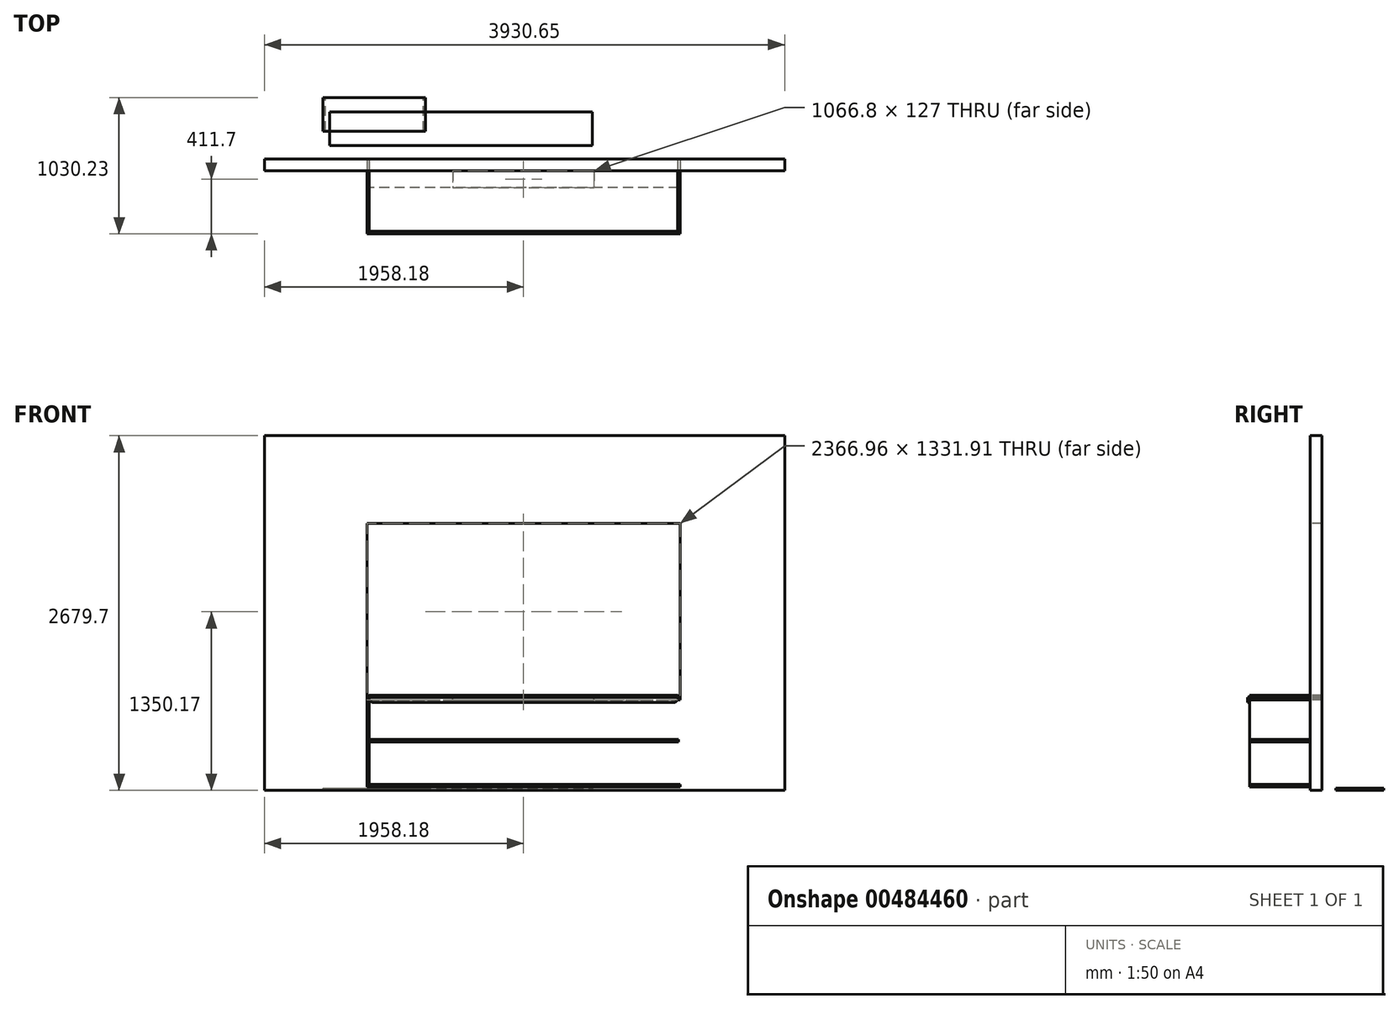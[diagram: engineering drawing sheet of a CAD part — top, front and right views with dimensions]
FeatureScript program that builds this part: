
annotation { "Feature Type Name" : "Feature", "Feature Type Description" : "" }
export const myFeature = defineFeature(function(context is Context, id is Id, definition is map)
    precondition{}
    {
        {
            assignVariable(context, id + "F0", {"name" : "windowwidth", "anyValue" : 2366.96 * mm});
        }
        {
            assignVariable(context, id + "F1", {"name" : "windowtofloor", "anyValue" : 684.2 * mm});
        }
        {
            assignVariable(context, id + "F2", {"name" : "materialthickness", "anyValue" : 18 * mm});
        }
        {
            assignVariable(context, id + "F3", {"name" : "trim", "anyValue" : 38.1 * mm});
        }
        {
            assignVariable(context, id + "F4", {"name" : "dadodepth", "anyValue" : getVariable(context, 'materialthickness') / 3});
        }
        {
            var Q0;
            Q0=qCreatedBy(makeId("Front.planeOp"),FACE);
            var sketch = newSketch(context, id + "F5", { "sketchPlane" : qUnion([Q0])});
            skLineSegment(sketch, "E0.bottom", {"start": v(-1875.03, 2679.7) * mm, "end": v(2055.62, 2679.7) * mm});
            skLineSegment(sketch, "E0.top", {"start": v(-1875.03, 0) * mm, "end": v(2055.62, 0) * mm});
            skLineSegment(sketch, "E0.left", {"start": v(-1875.03, 2679.7) * mm, "end": v(-1875.03, 0) * mm});
            skLineSegment(sketch, "E0.right", {"start": v(2055.62, 2679.7) * mm, "end": v(2055.62, 0) * mm});
            skSolve(sketch);
        }
        {
            var Q0;
            Q0 = qSketchRegion(id + "F5", true);
            extrude(context, id + "F6", {"entities" : qUnion([Q0]), "depth" : 88.9 * mm});
        }
        {
            var Q0;
            Q0=makeQuery(id+"F6.opExtrude","CAP_FACE",FACE,{"disambiguationData":[OSD([sQuery(id+"F5.wireOp",EDGE,"E0.bottom"),sQuery(id+"F5.wireOp",EDGE,"E0.top"),sQuery(id+"F5.wireOp",EDGE,"E0.left"),sQuery(id+"F5.wireOp",EDGE,"E0.right")])],"isStart":false});
            var sketch = newSketch(context, id + "F7", { "sketchPlane" : qUnion([Q0])});
            skLineSegment(sketch, "E1.bottom", {"start": v(-1100.33, 2016.13) * mm, "end": v(1266.63, 2016.13) * mm});
            skLineSegment(sketch, "E1.top", {"start": v(-1100.33, 684.21) * mm, "end": v(1266.63, 684.21) * mm});
            skLineSegment(sketch, "E1.left", {"start": v(-1100.33, 2016.12) * mm, "end": v(-1100.33, 684.21) * mm});
            skLineSegment(sketch, "E1.right", {"start": v(1266.63, 2016.12) * mm, "end": v(1266.63, 684.21) * mm});
            skSolve(sketch);
        }
        {
            var Q0;
            Q0 = qSketchRegion(id + "F7", true);
            extrude(context, id + "F8", {"entities" : qUnion([Q0]), "operationType" : NewBodyOperationType.REMOVE, "oppositeDirection" : true, "depth" : 101.6 * mm});
        }
        {
            var Q0;
            Q0=makeQuery(id+"F8.boolean.opBoolean","COPY",FACE,{"derivedFrom":makeQuery(id+"F8.opExtrude","SWEPT_FACE",FACE,{"disambiguationData":[OSD([sQuery(id+"F7.wireOp",EDGE,"E1.top")])]})});
            var sketch = newSketch(context, id + "F9", { "sketchPlane" : qUnion([Q0])});
            skPoint(sketch, "E2.oppositeSnap0", {"position": v(1266.63, -44.45) * mm});
            skLineSegment(sketch, "E2.bottom", {"start": v(-1100.33, 0) * mm, "end": v(1266.63, 0) * mm});
            skLineSegment(sketch, "E2.top", {"start": v(-1100.33, -546.1) * mm, "end": v(1266.63, -546.1) * mm});
            skLineSegment(sketch, "E2.left", {"start": v(-1100.33, 0) * mm, "end": v(-1100.33, -546.1) * mm});
            skLineSegment(sketch, "E2.right", {"start": v(1266.63, 0) * mm, "end": v(1266.63, -546.1) * mm});
            skSolve(sketch);
        }
        {
            var Q0;
            Q0 = qSketchRegion(id + "F9", true);
            extrude(context, id + "F10", {"entities" : qUnion([Q0]), "depth" : getVariable(context, 'materialthickness')});
        }
        {
            var Q0;
            Q0=makeQuery(id+"F10.opExtrude","CAP_FACE",FACE,{"disambiguationData":[OSD([sQuery(id+"F9.wireOp",EDGE,"E2.bottom"),sQuery(id+"F9.wireOp",EDGE,"E2.top"),sQuery(id+"F9.wireOp",EDGE,"E2.left"),sQuery(id+"F9.wireOp",EDGE,"E2.right")])],"isStart":true});
            var sketch = newSketch(context, id + "F11", { "sketchPlane" : qUnion([Q0])});
            skLineSegment(sketch, "E3.bottom", {"start": v(-1100.33, 546.1) * mm, "end": v(-1082.33, 546.1) * mm});
            skLineSegment(sketch, "E3.top", {"start": v(-1100.33, 0) * mm, "end": v(-1082.33, 0) * mm});
            skLineSegment(sketch, "E3.left", {"start": v(-1100.33, 546.1) * mm, "end": v(-1100.33, 0) * mm});
            skLineSegment(sketch, "E3.right", {"start": v(-1082.33, 546.1) * mm, "end": v(-1082.33, 0) * mm});
            skLineSegment(sketch, "E4.bottom", {"start": v(1266.63, 546.1) * mm, "end": v(1248.63, 546.1) * mm});
            skLineSegment(sketch, "E4.top", {"start": v(1266.63, 0) * mm, "end": v(1248.63, 0) * mm});
            skLineSegment(sketch, "E4.left", {"start": v(1266.63, 546.1) * mm, "end": v(1266.63, 0) * mm});
            skLineSegment(sketch, "E4.right", {"start": v(1248.63, 546.1) * mm, "end": v(1248.63, 0) * mm});
            skSolve(sketch);
        }
        {
            var Q0;
            Q0 = qSketchRegion(id + "F11", true);
            extrude(context, id + "F12", {"entities" : qUnion([Q0]), "operationType" : NewBodyOperationType.REMOVE, "oppositeDirection" : true, "depth" : getVariable(context, 'dadodepth')});
        }
        {
            var Q0;
            Q0=makeQuery(id+"F10.opExtrude","CAP_FACE",FACE,{"disambiguationData":[OSD([sQuery(id+"F9.wireOp",EDGE,"E2.bottom"),sQuery(id+"F9.wireOp",EDGE,"E2.top"),sQuery(id+"F9.wireOp",EDGE,"E2.left"),sQuery(id+"F9.wireOp",EDGE,"E2.right")])],"isStart":false});
            var sketch = newSketch(context, id + "F13", { "sketchPlane" : qUnion([Q0])});
            skLineSegment(sketch, "E5", {"start": v(83.15, -546.1) * mm, "end": v(83.15, 0) * mm, "construction": true});
            skLineSegment(sketch, "E6.bottom", {"start": v(-450.25, -88.9) * mm, "end": v(616.55, -88.9) * mm});
            skLineSegment(sketch, "E6.top", {"start": v(-450.25, -215.9) * mm, "end": v(616.55, -215.9) * mm});
            skLineSegment(sketch, "E6.left", {"start": v(-450.25, -88.9) * mm, "end": v(-450.25, -215.9) * mm});
            skLineSegment(sketch, "E6.right", {"start": v(616.55, -88.9) * mm, "end": v(616.55, -215.9) * mm});
            skPoint(sketch, "E6.middle", {"position": v(83.15, -273.05) * mm});
            skSolve(sketch);
        }
        {
            var Q0;
            Q0 = qSketchRegion(id + "F13", true);
            extrude(context, id + "F14", {"entities" : qUnion([Q0]), "operationType" : NewBodyOperationType.REMOVE, "oppositeDirection" : true, "depth" : 25.4 * mm});
        }
        {
            var Q0;
            Q0=makeQuery(id+"F12.boolean.opBoolean","COPY",FACE,{"derivedFrom":makeQuery(id+"F12.opExtrude","CAP_FACE",FACE,{"disambiguationData":[OSD([sQuery(id+"F11.wireOp",EDGE,"E3.bottom"),sQuery(id+"F11.wireOp",EDGE,"E3.top"),sQuery(id+"F11.wireOp",EDGE,"E3.left"),sQuery(id+"F11.wireOp",EDGE,"E3.right")])],"isStart":false})});
            var sketch = newSketch(context, id + "F15", { "sketchPlane" : qUnion([Q0])});
            skLineSegment(sketch, "E7.bottom", {"start": v(-1100.33, 546.1) * mm, "end": v(-1082.33, 546.1) * mm});
            skLineSegment(sketch, "E7.top", {"start": v(-1100.33, 88.9) * mm, "end": v(-1082.33, 88.9) * mm});
            skLineSegment(sketch, "E7.left", {"start": v(-1100.33, 546.1) * mm, "end": v(-1100.33, 88.9) * mm});
            skLineSegment(sketch, "E7.right", {"start": v(-1082.33, 546.1) * mm, "end": v(-1082.33, 88.9) * mm});
            skSolve(sketch);
        }
        {
            var Q0;
            Q0 = qSketchRegion(id + "F15", true);
            extrude(context, id + "F16", {"entities" : qUnion([Q0]), "depth" : getVariable(context, 'windowtofloor') + getVariable(context, 'dadodepth') - (getVariable(context, 'materialthickness') - getVariable(context, 'dadodepth')) - (getVariable(context, 'trim') - getVariable(context, 'dadodepth'))});
        }
        {
            var Q0;
            Q0=makeQuery(id+"F10.opExtrude","SWEPT_FACE",FACE,{"disambiguationData":[OSD([sQuery(id+"F9.wireOp",EDGE,"E2.top")])]});
            var sketch = newSketch(context, id + "F17", { "sketchPlane" : qUnion([Q0])});
            skLineSegment(sketch, "E8", {"start": v(-1100.33, 702.21) * mm, "end": v(1266.63, 702.21) * mm});
            skLineSegment(sketch, "E9", {"start": v(1266.63, 702.21) * mm, "end": v(1228.53, 664.11) * mm});
            skLineSegment(sketch, "E10", {"start": v(-1100.33, 702.21) * mm, "end": v(-1062.23, 664.11) * mm});
            skLineSegment(sketch, "E11", {"start": v(-1062.23, 664.11) * mm, "end": v(1228.53, 664.11) * mm});
            skSolve(sketch);
        }
        {
            var Q0;
            Q0 = qSketchRegion(id + "F17", true);
            extrude(context, id + "F18", {"entities" : qUnion([Q0]), "depth" : getVariable(context, 'materialthickness')});
        }
        {
            var Q0;
            Q0=makeQuery(id+"F16.opExtrude","SWEPT_FACE",FACE,{"disambiguationData":[OSD([sQuery(id+"F15.wireOp",EDGE,"E7.right")])]});
            var sketch = newSketch(context, id + "F19", { "sketchPlane" : qUnion([Q0])});
            skLineSegment(sketch, "E12.bottom", {"start": v(-546.1, 385.16) * mm, "end": v(-88.9, 385.16) * mm});
            skLineSegment(sketch, "E12.top", {"start": v(-546.1, 367.16) * mm, "end": v(-88.9, 367.16) * mm});
            skLineSegment(sketch, "E12.left", {"start": v(-546.1, 385.16) * mm, "end": v(-546.1, 367.16) * mm});
            skLineSegment(sketch, "E12.right", {"start": v(-88.9, 385.16) * mm, "end": v(-88.9, 367.16) * mm});
            skSolve(sketch);
        }
        {
            var Q0;
            Q0 = qSketchRegion(id + "F19", true);
            extrude(context, id + "F20", {"entities" : qUnion([Q0]), "operationType" : NewBodyOperationType.REMOVE, "oppositeDirection" : true, "depth" : getVariable(context, 'dadodepth')});
        }
        {
            var Q0;
            Q0=makeQuery(id+"F20.boolean.opBoolean","COPY",FACE,{"derivedFrom":makeQuery(id+"F20.opExtrude","CAP_FACE",FACE,{"disambiguationData":[OSD([sQuery(id+"F19.wireOp",EDGE,"E12.bottom"),sQuery(id+"F19.wireOp",EDGE,"E12.top"),sQuery(id+"F19.wireOp",EDGE,"E12.left"),sQuery(id+"F19.wireOp",EDGE,"E12.right")])],"isStart":false})});
            var sketch = newSketch(context, id + "F21", { "sketchPlane" : qUnion([Q0])});
            skLineSegment(sketch, "E13.bottom", {"start": v(-546.1, 385.16) * mm, "end": v(-215.9, 385.16) * mm});
            skLineSegment(sketch, "E13.top", {"start": v(-546.1, 367.16) * mm, "end": v(-215.9, 367.16) * mm});
            skLineSegment(sketch, "E13.left", {"start": v(-546.1, 385.16) * mm, "end": v(-546.1, 367.16) * mm});
            skLineSegment(sketch, "E13.right", {"start": v(-215.9, 385.16) * mm, "end": v(-215.9, 367.16) * mm});
            skSolve(sketch);
        }
        {
            var Q0;
            Q0 = qSketchRegion(id + "F21", true);
            extrude(context, id + "F22", {"entities" : qUnion([Q0]), "depth" : getVariable(context, 'windowwidth') - 2 * getVariable(context, 'materialthickness') + 2 * getVariable(context, 'dadodepth')});
        }
        {
            var Q0;
            Q0=makeQuery(id+"F6.opExtrude","SWEPT_FACE",FACE,{"disambiguationData":[OSD([sQuery(id+"F5.wireOp",EDGE,"E0.top")])]});
            var sketch = newSketch(context, id + "F23", { "sketchPlane" : qUnion([Q0])});
            skLineSegment(sketch, "E14.bottom", {"start": v(-1101.17, 88.9) * mm, "end": v(1265.8, 88.9) * mm});
            skLineSegment(sketch, "E14.top", {"start": v(-1101.17, 546.1) * mm, "end": v(1265.8, 546.1) * mm});
            skLineSegment(sketch, "E14.left", {"start": v(-1101.17, 88.9) * mm, "end": v(-1101.17, 546.1) * mm});
            skLineSegment(sketch, "E14.right", {"start": v(1265.8, 88.9) * mm, "end": v(1265.8, 546.1) * mm});
            skSolve(sketch);
        }
        {
            var Q0;
            Q0 = qSketchRegion(id + "F23", true);
            extrude(context, id + "F24", {"entities" : qUnion([Q0]), "oppositeDirection" : true, "depth" : getVariable(context, 'materialthickness')});
        }
        {
            var Q0;
            Q0=makeQuery(id+"F24.opExtrude","SWEPT_BODY",BODY,{"disambiguationData":[OSD([sQuery(id+"F23.wireOp",EDGE,"E14.bottom"),sQuery(id+"F23.wireOp",EDGE,"E14.top"),sQuery(id+"F23.wireOp",EDGE,"E14.left"),sQuery(id+"F23.wireOp",EDGE,"E14.right")])]});
            deleteBodies(context, id + "F25", {"entities" : qUnion([Q0])});
        }
        {
            var Q0;
            Q0=makeQuery(id+"F10.opExtrude","CAP_FACE",FACE,{"disambiguationData":[OSD([sQuery(id+"F9.wireOp",EDGE,"E2.bottom"),sQuery(id+"F9.wireOp",EDGE,"E2.top"),sQuery(id+"F9.wireOp",EDGE,"E2.left"),sQuery(id+"F9.wireOp",EDGE,"E2.right")])],"isStart":false});
            var sketch = newSketch(context, id + "F26", { "sketchPlane" : qUnion([Q0])});
            skLineSegment(sketch, "E15.bottom", {"start": v(-1100.33, 0) * mm, "end": v(1266.63, 0) * mm});
            skLineSegment(sketch, "E15.top", {"start": v(-1100.33, -546.1) * mm, "end": v(1266.63, -546.1) * mm});
            skLineSegment(sketch, "E15.left", {"start": v(-1100.33, 0) * mm, "end": v(-1100.33, -546.1) * mm});
            skLineSegment(sketch, "E15.right", {"start": v(1266.63, 0) * mm, "end": v(1266.63, -546.1) * mm});
            skSolve(sketch);
        }
        {
            var Q0;
            Q0 = qSketchRegion(id + "F26", true);
            extrude(context, id + "F27", {"entities" : qUnion([Q0]), "depth" : getVariable(context, 'materialthickness')});
        }
        {
            var Q0;
            Q0=makeQuery(id+"F27.opExtrude","CAP_FACE",FACE,{"disambiguationData":[OSD([sQuery(id+"F26.wireOp",EDGE,"E15.bottom"),sQuery(id+"F26.wireOp",EDGE,"E15.top"),sQuery(id+"F26.wireOp",EDGE,"E15.left"),sQuery(id+"F26.wireOp",EDGE,"E15.right")])],"isStart":false});
            var sketch = newSketch(context, id + "F28", { "sketchPlane" : qUnion([Q0])});
            skLineSegment(sketch, "E16.bottom", {"start": v(-1100.33, 0) * mm, "end": v(-1082.33, 0) * mm});
            skLineSegment(sketch, "E16.top", {"start": v(-1100.33, -546.1) * mm, "end": v(-1082.33, -546.1) * mm});
            skLineSegment(sketch, "E16.left", {"start": v(-1100.33, 0) * mm, "end": v(-1100.33, -546.1) * mm});
            skLineSegment(sketch, "E16.right", {"start": v(-1082.33, 0) * mm, "end": v(-1082.33, -546.1) * mm});
            skLineSegment(sketch, "E17.bottom", {"start": v(1266.63, 0) * mm, "end": v(1248.63, 0) * mm});
            skLineSegment(sketch, "E17.top", {"start": v(1266.63, -546.1) * mm, "end": v(1248.63, -546.1) * mm});
            skLineSegment(sketch, "E17.left", {"start": v(1266.63, 0) * mm, "end": v(1266.63, -546.1) * mm});
            skLineSegment(sketch, "E17.right", {"start": v(1248.63, 0) * mm, "end": v(1248.63, -546.1) * mm});
            skSolve(sketch);
        }
        {
            var Q0;
            Q0 = qSketchRegion(id + "F28", true);
            extrude(context, id + "F29", {"entities" : qUnion([Q0]), "operationType" : NewBodyOperationType.REMOVE, "oppositeDirection" : true, "depth" : getVariable(context, 'dadodepth')});
        }
        {
            var Q0;
            Q0=qCreatedBy(makeId("Top.planeOp"),FACE);
            var sketch = newSketch(context, id + "F30", { "sketchPlane" : qUnion([Q0])});
            skLineSegment(sketch, "E18.bottom", {"start": v(-1431.35, 212.13) * mm, "end": v(-656.65, 212.13) * mm});
            skLineSegment(sketch, "E18.top", {"start": v(-1431.35, 466.13) * mm, "end": v(-656.65, 466.13) * mm});
            skLineSegment(sketch, "E18.left", {"start": v(-1431.35, 212.13) * mm, "end": v(-1431.35, 466.13) * mm});
            skLineSegment(sketch, "E18.right", {"start": v(-656.65, 212.13) * mm, "end": v(-656.65, 466.13) * mm});
            skSolve(sketch);
        }
        {
            var Q0;
            Q0 = qSketchRegion(id + "F30", true);
            extrude(context, id + "F31", {"entities" : qUnion([Q0]), "depth" : getVariable(context, 'materialthickness')});
        }
        {
            var Q0;
            Q0=makeQuery(id+"F31.opExtrude","CAP_FACE",FACE,{"disambiguationData":[OSD([sQuery(id+"F30.wireOp",EDGE,"E18.bottom"),sQuery(id+"F30.wireOp",EDGE,"E18.top"),sQuery(id+"F30.wireOp",EDGE,"E18.left"),sQuery(id+"F30.wireOp",EDGE,"E18.right")])],"isStart":true});
            var sketch = newSketch(context, id + "F32", { "sketchPlane" : qUnion([Q0])});
            skLineSegment(sketch, "E19.bottom", {"start": v(-1431.35, -212.13) * mm, "end": v(-1413.35, -212.13) * mm});
            skLineSegment(sketch, "E19.top", {"start": v(-1431.35, -466.13) * mm, "end": v(-1413.35, -466.13) * mm});
            skLineSegment(sketch, "E19.left", {"start": v(-1431.35, -212.13) * mm, "end": v(-1431.35, -466.13) * mm});
            skLineSegment(sketch, "E19.right", {"start": v(-1413.35, -212.13) * mm, "end": v(-1413.35, -466.13) * mm});
            skLineSegment(sketch, "E20.bottom", {"start": v(-656.65, -212.13) * mm, "end": v(-674.65, -212.13) * mm});
            skLineSegment(sketch, "E20.top", {"start": v(-656.65, -466.13) * mm, "end": v(-674.65, -466.13) * mm});
            skLineSegment(sketch, "E20.left", {"start": v(-656.65, -212.13) * mm, "end": v(-656.65, -466.13) * mm});
            skLineSegment(sketch, "E20.right", {"start": v(-674.65, -212.13) * mm, "end": v(-674.65, -466.13) * mm});
            skSolve(sketch);
        }
        {
            var Q0;
            Q0 = qSketchRegion(id + "F32", true);
            extrude(context, id + "F33", {"entities" : qUnion([Q0]), "operationType" : NewBodyOperationType.REMOVE, "oppositeDirection" : true, "depth" : getVariable(context, 'dadodepth')});
        }
        {
            var Q0;
            Q0=qCreatedBy(makeId("Top.planeOp"),FACE);
            var sketch = newSketch(context, id + "F34", { "sketchPlane" : qUnion([Q0])});
            skLineSegment(sketch, "E21.bottom", {"start": v(-1380.04, 103.64) * mm, "end": v(603.45, 103.64) * mm});
            skLineSegment(sketch, "E21.top", {"start": v(-1380.04, 357.64) * mm, "end": v(603.45, 357.64) * mm});
            skLineSegment(sketch, "E21.left", {"start": v(-1380.04, 103.64) * mm, "end": v(-1380.04, 357.64) * mm});
            skLineSegment(sketch, "E21.right", {"start": v(603.45, 103.64) * mm, "end": v(603.45, 357.64) * mm});
            skSolve(sketch);
        }
        {
            var Q0;
            Q0 = qSketchRegion(id + "F34", true);
            extrude(context, id + "F35", {"entities" : qUnion([Q0]), "depth" : getVariable(context, 'materialthickness')});
        }
        {
            var Q0;
            Q0=makeQuery(id+"F16.opExtrude","CAP_FACE",FACE,{"disambiguationData":[OSD([sQuery(id+"F15.wireOp",EDGE,"E7.bottom"),sQuery(id+"F15.wireOp",EDGE,"E7.top"),sQuery(id+"F15.wireOp",EDGE,"E7.left"),sQuery(id+"F15.wireOp",EDGE,"E7.right")])],"isStart":false});
            var sketch = newSketch(context, id + "F36", { "sketchPlane" : qUnion([Q0])});
            skLineSegment(sketch, "E22.0", {"start": v(-1100.33, 546.1) * mm, "end": v(1266.63, 546.1) * mm});
            skLineSegment(sketch, "E23.0", {"start": v(-1100.33, 88.9) * mm, "end": v(1266.63, 88.9) * mm});
            skLineSegment(sketch, "E24.0", {"start": v(-1100.33, 88.9) * mm, "end": v(-1100.33, 546.1) * mm});
            skLineSegment(sketch, "E25.0", {"start": v(1266.63, 88.9) * mm, "end": v(1266.63, 546.1) * mm});
            skPoint(sketch, "E26.orphan", {"position": v(1266.63, 0) * mm});
            skSolve(sketch);
        }
        {
            var Q0;
            Q0 = qSketchRegion(id + "F36", true);
            extrude(context, id + "F37", {"entities" : qUnion([Q0]), "depth" : getVariable(context, 'materialthickness')});
        }
    });
